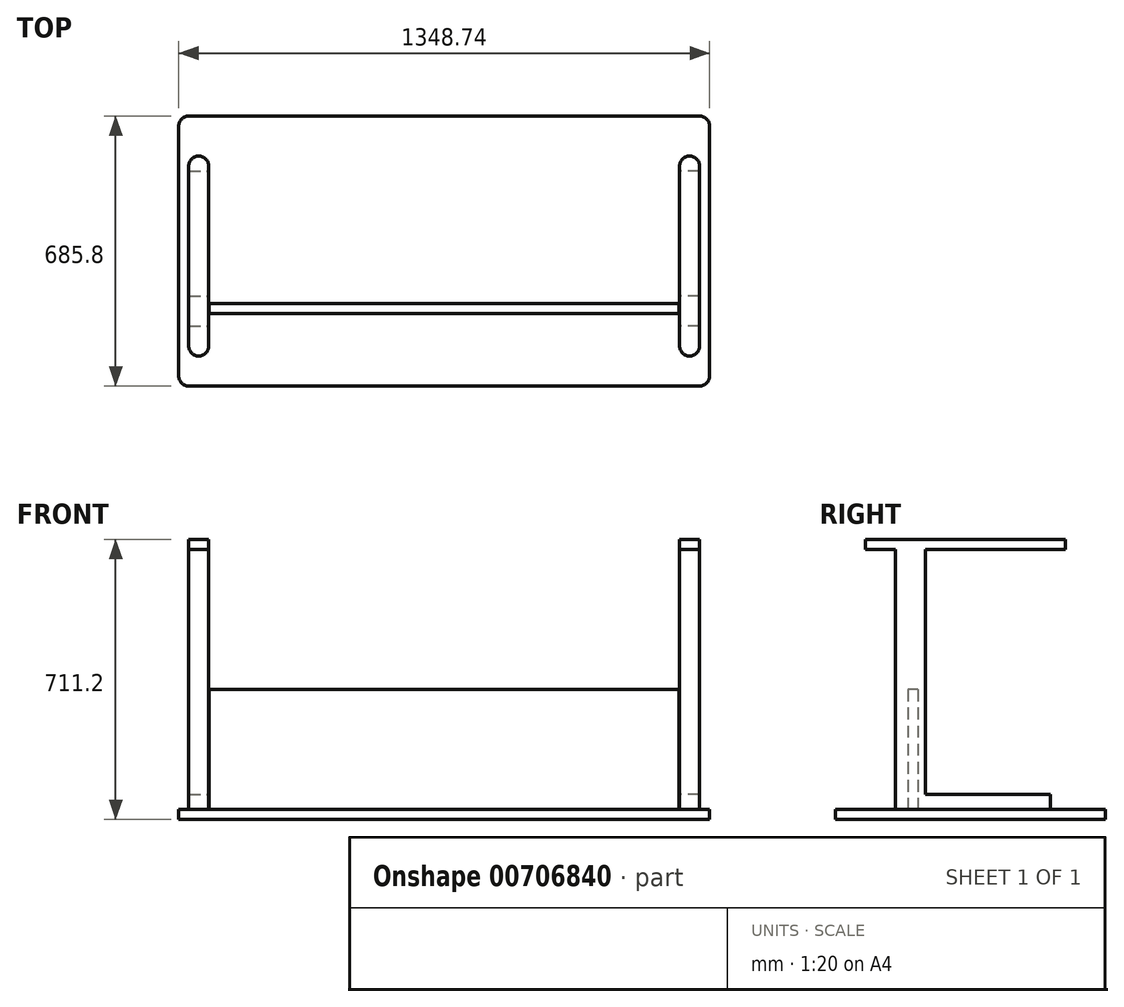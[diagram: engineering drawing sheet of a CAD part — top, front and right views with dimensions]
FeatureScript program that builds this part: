
annotation { "Feature Type Name" : "Feature", "Feature Type Description" : "" }
export const myFeature = defineFeature(function(context is Context, id is Id, definition is map)
    precondition{}
    {
        {
            var Q0;
            Q0=qCreatedBy(makeId("Top.planeOp"),FACE);
            var sketch = newSketch(context, id + "F0", { "sketchPlane" : qUnion([Q0])});
            skLineSegment(sketch, "E0.bottom", {"start": v(-674.37, 342.9) * mm, "end": v(674.37, 342.9) * mm});
            skLineSegment(sketch, "E0.top", {"start": v(-674.37, -342.9) * mm, "end": v(674.37, -342.9) * mm});
            skLineSegment(sketch, "E0.left", {"start": v(-674.37, 342.9) * mm, "end": v(-674.37, -342.9) * mm});
            skLineSegment(sketch, "E0.right", {"start": v(674.37, 342.9) * mm, "end": v(674.37, -342.9) * mm});
            skPoint(sketch, "E0.middle", {"position": v(0, 0) * mm});
            skSolve(sketch);
        }
        {
            var Q0;
            Q0=makeQuery(id+"F0.imprint","IMPRINT",FACE,{"disambiguationData":[TD([[makeQuery(id+"F0.imprint","IMPRINT",EDGE,{"derivedFrom":sQuery(id+"F0.wireOp",EDGE,"E0.bottom")}),-1.0]])]});
            extrude(context, id + "F1", {"entities" : qUnion([Q0]), "depth" : 25.4 * mm, "offsetDistance" : 25.4 * mm});
        }
        {
            var Q0;
            Q0=makeQuery(id+"F1.opExtrude","CAP_FACE",FACE,{"disambiguationData":[OSD([sQuery(id+"F0.wireOp",EDGE,"E0.bottom"),sQuery(id+"F0.wireOp",EDGE,"E0.top"),sQuery(id+"F0.wireOp",EDGE,"E0.left"),sQuery(id+"F0.wireOp",EDGE,"E0.right")])],"isStart":false});
            var sketch = newSketch(context, id + "F2", { "sketchPlane" : qUnion([Q0])});
            skLineSegment(sketch, "E1", {"start": v(0, 0) * mm, "end": v(0, 342.9) * mm});
            skLineSegment(sketch, "E2", {"start": v(0, 0) * mm, "end": v(0, -342.9) * mm});
            skSolve(sketch);
        }
        {
            var Q0;
            {var subQ2=sQuery(id+"F2.wireOp",EDGE,"E1");Q0=makeQuery(id+"F2.imprint","IMPRINT",FACE,{"disambiguationData":[TD([[makeQuery(id+"F2.imprint","IMPRINT",EDGE,{"derivedFrom":subQ2}),1.0]])]});}
            var sketch = newSketch(context, id + "F3", { "sketchPlane" : qUnion([Q0])});
            skLineSegment(sketch, "E3.bottom", {"start": v(-648.97, 203.2) * mm, "end": v(-598.17, 203.2) * mm});
            skLineSegment(sketch, "E3.top", {"start": v(-648.97, -114.3) * mm, "end": v(-598.17, -114.3) * mm});
            skLineSegment(sketch, "E3.left", {"start": v(-648.97, 203.2) * mm, "end": v(-648.97, -114.3) * mm});
            skLineSegment(sketch, "E3.right", {"start": v(-598.17, 203.2) * mm, "end": v(-598.17, -114.3) * mm});
            skLineSegment(sketch, "E4.MirrorCS", {"start": v(598.17, 203.2) * mm, "end": v(598.17, -114.3) * mm});
            skLineSegment(sketch, "E5.MirrorCS", {"start": v(648.97, 203.2) * mm, "end": v(598.17, 203.2) * mm});
            skLineSegment(sketch, "E6.MirrorCS", {"start": v(648.97, 203.2) * mm, "end": v(648.97, -114.3) * mm});
            skLineSegment(sketch, "E7.MirrorCS", {"start": v(648.97, -114.3) * mm, "end": v(598.17, -114.3) * mm});
            skSolve(sketch);
        }
        {
            var Q0;
            Q0=qSketchRegion(id+"F3",true);
            extrude(context, id + "F4", {"entities" : qUnion([Q0]), "operationType" : NewBodyOperationType.ADD, "depth" : 38.1 * mm, "offsetDistance" : 25.4 * mm});
        }
        {
            var Q0;
            {var subQ2=sQuery(id+"F2.wireOp",EDGE,"E1");Q0=makeQuery(id+"F2.imprint","IMPRINT",FACE,{"disambiguationData":[TD([[makeQuery(id+"F2.imprint","IMPRINT",EDGE,{"derivedFrom":subQ2}),1.0]])]});}
            var sketch = newSketch(context, id + "F5", { "sketchPlane" : qUnion([Q0])});
            skLineSegment(sketch, "E8.bottom", {"start": v(-648.97, -114.3) * mm, "end": v(-598.17, -114.3) * mm});
            skLineSegment(sketch, "E8.top", {"start": v(-648.97, -190.5) * mm, "end": v(-598.17, -190.5) * mm});
            skLineSegment(sketch, "E8.left", {"start": v(-648.97, -114.3) * mm, "end": v(-648.97, -190.5) * mm});
            skLineSegment(sketch, "E8.right", {"start": v(-598.17, -114.3) * mm, "end": v(-598.17, -190.5) * mm});
            skLineSegment(sketch, "E9.MirrorCS", {"start": v(648.97, -190.5) * mm, "end": v(598.17, -190.5) * mm});
            skLineSegment(sketch, "E10.MirrorCS", {"start": v(648.97, -114.3) * mm, "end": v(648.97, -190.5) * mm});
            skLineSegment(sketch, "E11.MirrorCS", {"start": v(598.17, -114.3) * mm, "end": v(598.17, -190.5) * mm});
            skLineSegment(sketch, "E12.MirrorCS", {"start": v(648.97, -114.3) * mm, "end": v(598.17, -114.3) * mm});
            skSolve(sketch);
        }
        {
            var Q0;
            Q0=qSketchRegion(id+"F5",true);
            extrude(context, id + "F6", {"entities" : qUnion([Q0]), "operationType" : NewBodyOperationType.ADD, "depth" : 660.4 * mm, "offsetDistance" : 25.4 * mm});
        }
        {
            var Q0;
            Q0=makeQuery(id+"F6.opExtrude","CAP_FACE",FACE,{"disambiguationData":[OSD([sQuery(id+"F5.wireOp",EDGE,"E8.bottom"),sQuery(id+"F5.wireOp",EDGE,"E8.top"),sQuery(id+"F5.wireOp",EDGE,"E8.left"),sQuery(id+"F5.wireOp",EDGE,"E8.right")])],"isStart":false});
            var sketch = newSketch(context, id + "F7", { "sketchPlane" : qUnion([Q0])});
            skLineSegment(sketch, "E13.bottom", {"start": v(-623.57, 241.3) * mm, "end": v(-623.57, 241.3) * mm});
            skLineSegment(sketch, "E13.top", {"start": v(-623.57, -266.7) * mm, "end": v(-623.57, -266.7) * mm});
            skLineSegment(sketch, "E13.left", {"start": v(-648.97, 215.9) * mm, "end": v(-648.97, -241.3) * mm});
            skLineSegment(sketch, "E13.right", {"start": v(-598.17, 215.9) * mm, "end": v(-598.17, -241.3) * mm});
            skPoint(sketch, "E14.visualSharp", {"position": v(-648.97, 241.3) * mm});
            skArc(sketch, "E14.filletArc", {"start": v(-623.57, 241.3) * mm, "mid": v(-641.53, 233.86) * mm, "end": v(-648.97, 215.9) * mm});
            skPoint(sketch, "E15.visualSharp", {"position": v(-598.17, 241.3) * mm});
            skArc(sketch, "E15.filletArc", {"start": v(-598.17, 215.9) * mm, "mid": v(-605.6, 233.86) * mm, "end": v(-623.57, 241.3) * mm});
            skPoint(sketch, "E16.visualSharp", {"position": v(-648.97, -266.7) * mm});
            skArc(sketch, "E16.filletArc", {"start": v(-648.97, -241.3) * mm, "mid": v(-641.53, -259.26) * mm, "end": v(-623.57, -266.7) * mm});
            skPoint(sketch, "E17.visualSharp", {"position": v(-598.17, -266.7) * mm});
            skArc(sketch, "E17.filletArc", {"start": v(-623.57, -266.7) * mm, "mid": v(-605.6, -259.26) * mm, "end": v(-598.17, -241.3) * mm});
            skLineSegment(sketch, "E18.MirrorCS", {"start": v(648.97, 215.9) * mm, "end": v(648.97, -241.3) * mm});
            skLineSegment(sketch, "E19.MirrorCS", {"start": v(598.17, 215.9) * mm, "end": v(598.17, -241.3) * mm});
            skArc(sketch, "E20.MirrorCS", {"start": v(648.97, -241.3) * mm, "mid": v(641.53, -259.26) * mm, "end": v(623.57, -266.7) * mm});
            skArc(sketch, "E21.MirrorCS", {"start": v(623.57, -266.7) * mm, "mid": v(605.6, -259.26) * mm, "end": v(598.17, -241.3) * mm});
            skArc(sketch, "E22.MirrorCS", {"start": v(598.17, 215.9) * mm, "mid": v(605.6, 233.86) * mm, "end": v(623.57, 241.3) * mm});
            skArc(sketch, "E23.MirrorCS", {"start": v(623.57, 241.3) * mm, "mid": v(641.53, 233.86) * mm, "end": v(648.97, 215.9) * mm});
            skSolve(sketch);
        }
        {
            var Q0;
            Q0=qSketchRegion(id+"F7",true);
            extrude(context, id + "F8", {"entities" : qUnion([Q0]), "operationType" : NewBodyOperationType.ADD, "depth" : 25.4 * mm, "offsetDistance" : 25.4 * mm});
        }
        {
            var Q0;
            {var subQ2=sQuery(id+"F2.wireOp",EDGE,"E1");Q0=makeQuery(id+"F2.imprint","IMPRINT",FACE,{"disambiguationData":[TD([[makeQuery(id+"F2.imprint","IMPRINT",EDGE,{"derivedFrom":subQ2}),1.0]])]});}
            var sketch = newSketch(context, id + "F9", { "sketchPlane" : qUnion([Q0])});
            skLineSegment(sketch, "E24.bottom", {"start": v(-597.54, -133.17) * mm, "end": v(597.13, -133.17) * mm});
            skLineSegment(sketch, "E24.top", {"start": v(-597.54, -158.76) * mm, "end": v(597.13, -158.76) * mm});
            skLineSegment(sketch, "E24.left", {"start": v(-597.54, -133.17) * mm, "end": v(-597.54, -158.76) * mm});
            skLineSegment(sketch, "E24.right", {"start": v(597.13, -133.17) * mm, "end": v(597.13, -158.76) * mm});
            skSolve(sketch);
        }
        {
            var Q0;
            Q0=qSketchRegion(id+"F9",true);
            extrude(context, id + "F10", {"entities" : qUnion([Q0]), "operationType" : NewBodyOperationType.ADD, "depth" : 304.8 * mm, "offsetDistance" : 25.4 * mm});
        }
        {
            var Q0;
            Q0=makeQuery(id+"F1.opExtrude","SWEPT_EDGE",EDGE,{"disambiguationData":[OSD([sQuery(id+"F0.wireOp",EDGE,"E0.bottom"),sQuery(id+"F0.wireOp",EDGE,"E0.left")])]});
            fillet(context, id + "F11", {"entities" : qUnion([Q0]), "radius" : 25.4 * mm, "tangentPropagation" : true, "allowEdgeOverflow" : false});
        }
        {
            var Q0;
            Q0=makeQuery(id+"F1.opExtrude","SWEPT_EDGE",EDGE,{"disambiguationData":[OSD([sQuery(id+"F0.wireOp",EDGE,"E0.top"),sQuery(id+"F0.wireOp",EDGE,"E0.left")])]});
            fillet(context, id + "F12", {"entities" : qUnion([Q0]), "radius" : 25.4 * mm, "tangentPropagation" : true, "allowEdgeOverflow" : false});
        }
        {
            var Q0;
            Q0=makeQuery(id+"F1.opExtrude","SWEPT_EDGE",EDGE,{"disambiguationData":[OSD([sQuery(id+"F0.wireOp",EDGE,"E0.top"),sQuery(id+"F0.wireOp",EDGE,"E0.right")])]});
            fillet(context, id + "F13", {"entities" : qUnion([Q0]), "radius" : 25.4 * mm, "tangentPropagation" : true, "allowEdgeOverflow" : false});
        }
        {
            var Q0;
            Q0=makeQuery(id+"F1.opExtrude","SWEPT_EDGE",EDGE,{"disambiguationData":[OSD([sQuery(id+"F0.wireOp",EDGE,"E0.bottom"),sQuery(id+"F0.wireOp",EDGE,"E0.right")])]});
            fillet(context, id + "F14", {"entities" : qUnion([Q0]), "radius" : 25.4 * mm, "tangentPropagation" : true, "allowEdgeOverflow" : false});
        }
    });
